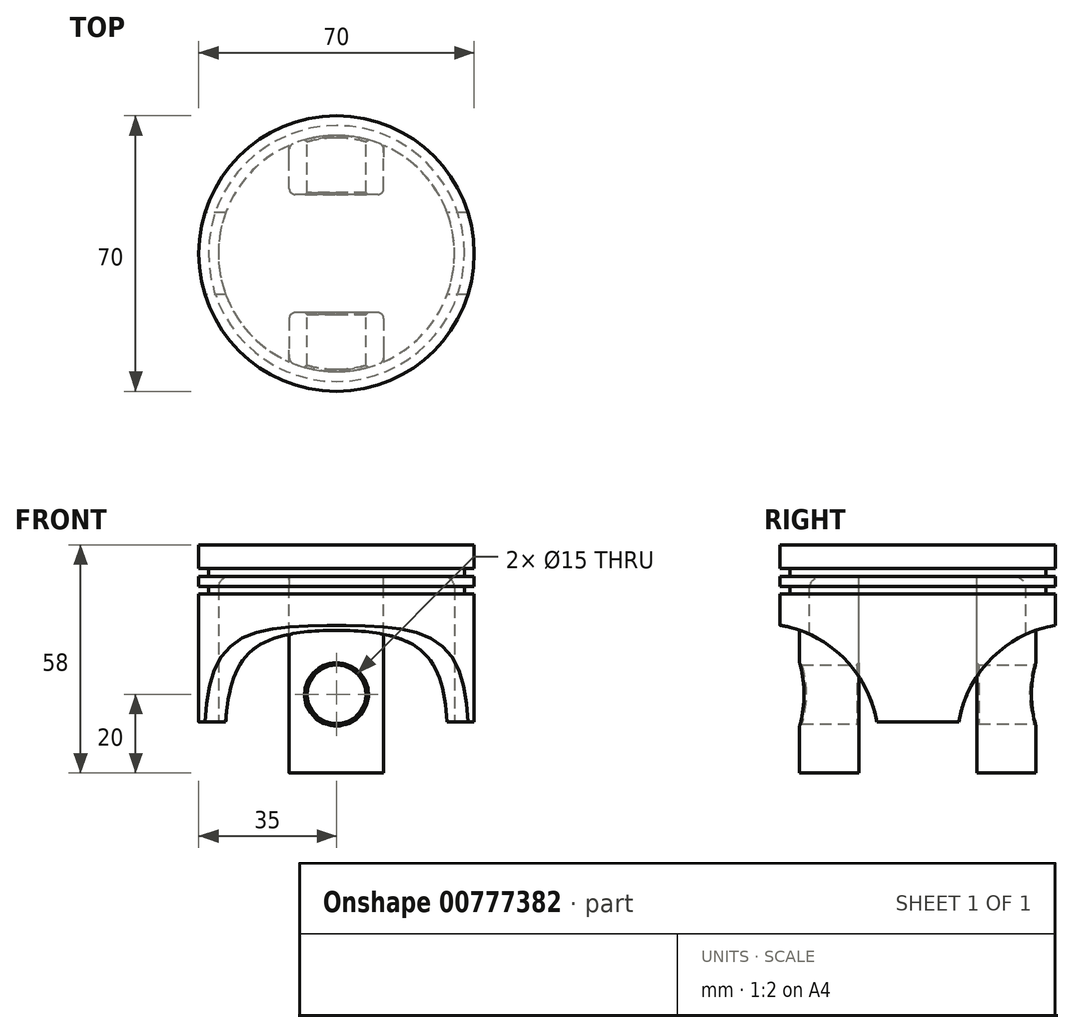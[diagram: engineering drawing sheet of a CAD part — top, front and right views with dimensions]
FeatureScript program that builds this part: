
annotation { "Feature Type Name" : "Feature", "Feature Type Description" : "" }
export const myFeature = defineFeature(function(context is Context, id is Id, definition is map)
    precondition{}
    {
        {
            var Q0;
            Q0=qCreatedBy(makeId("Front.planeOp"),FACE);
            var sketch = newSketch(context, id + "F0", { "sketchPlane" : qUnion([Q0])});
            skLineSegment(sketch, "E0", {"start": v(0, 0) * mm, "end": v(0, 45) * mm});
            skLineSegment(sketch, "E1", {"start": v(0, 45) * mm, "end": v(-35, 45) * mm});
            skLineSegment(sketch, "E2", {"start": v(-35, 45) * mm, "end": v(-35, 39) * mm});
            skLineSegment(sketch, "E3", {"start": v(-35, 0) * mm, "end": v(-30, 0) * mm});
            skLineSegment(sketch, "E4", {"start": v(-30, 0) * mm, "end": v(-30, 37) * mm});
            skLineSegment(sketch, "E5", {"start": v(-30, 37) * mm, "end": v(0, 37) * mm});
            skLineSegment(sketch, "E6", {"start": v(-35, 39) * mm, "end": v(-32.5, 39) * mm});
            skLineSegment(sketch, "E7", {"start": v(-32.5, 39) * mm, "end": v(-32.5, 37) * mm});
            skLineSegment(sketch, "E8", {"start": v(-32.5, 37) * mm, "end": v(-35, 37) * mm});
            skLineSegment(sketch, "E9", {"start": v(-35, 34.47) * mm, "end": v(-32.5, 34.47) * mm});
            skLineSegment(sketch, "E10", {"start": v(-32.5, 34.47) * mm, "end": v(-32.5, 32.47) * mm});
            skLineSegment(sketch, "E11", {"start": v(-32.5, 32.47) * mm, "end": v(-35, 32.47) * mm});
            skLineSegment(sketch, "E12.trimOffspring", {"start": v(-35, 32.47) * mm, "end": v(-35, 0) * mm});
            skLineSegment(sketch, "E13.trimOffspring", {"start": v(-35, 37) * mm, "end": v(-35, 34.47) * mm});
            skSolve(sketch);
        }
        {
            var Q0;
            Q0 = qSketchRegion(id + "F0", true);
            var Q1;
            Q1=sQuery(id+"F0.wireOp",EDGE,"E0");
            revolve(context, id + "F1", {"surfaceOperationType" : NewSurfaceOperationType.NEW, "entities" : qUnion([Q0]), "axis" : qUnion([Q1]), "revolveType" : RevolveType.FULL});
        }
        {
            var Q0;
            Q0=qCreatedBy(makeId("Right.planeOp"),FACE);
            var sketch = newSketch(context, id + "F2", { "sketchPlane" : qUnion([Q0])});
            skLineSegment(sketch, "E14", {"start": v(0, 0) * mm, "end": v(35, 0) * mm, "construction": true});
            skCircle(sketch, "E15", {"center": v(40, -5) * mm, "radius": 30 * mm});
            skLineSegment(sketch, "E16", {"start": v(0, 0) * mm, "end": v(0, 45) * mm, "construction": true});
            skCircle(sketch, "E17.MirrorC", {"center": v(-40, -5) * mm, "radius": 30 * mm});
            skSolve(sketch);
        }
        {
            var Q0;
            Q0 = qSketchRegion(id + "F2", true);
            extrude(context, id + "F3", {"entities" : qUnion([Q0]), "operationType" : NewBodyOperationType.REMOVE, "endBound" : BoundingType.THROUGH_ALL, "depth" : 80 * mm, "offsetDistance" : 25 * mm, "hasSecondDirection" : true, "secondDirectionBound" : BoundingType.THROUGH_ALL, "secondDirectionOppositeDirection" : true, "secondDirectionDepth" : 25 * mm});
        }
        {
            var Q0;
            Q0=makeQuery(id+"F1.opRevolve","SWEPT_FACE",FACE,{"disambiguationData":[OSD([sQuery(id+"F0.wireOp",EDGE,"E5")])]});
            var sketch = newSketch(context, id + "F4", { "sketchPlane" : qUnion([Q0])});
            skLineSegment(sketch, "E18", {"start": v(0, 0) * mm, "end": v(0, 30) * mm, "construction": true});
            skLineSegment(sketch, "E19", {"start": v(0, 0) * mm, "end": v(0, -30) * mm, "construction": true});
            skLineSegment(sketch, "E20", {"start": v(0, 0) * mm, "end": v(-30, 0) * mm, "construction": true});
            skLineSegment(sketch, "E21", {"start": v(0, 0) * mm, "end": v(30, 0) * mm, "construction": true});
            skLineSegment(sketch, "E22", {"start": v(0, 15) * mm, "end": v(-12, 15) * mm});
            skLineSegment(sketch, "E23", {"start": v(-12, 15) * mm, "end": v(-12, 27.5) * mm});
            skLineSegment(sketch, "E24.MirrorCS", {"start": v(0, 15) * mm, "end": v(12, 15) * mm});
            skLineSegment(sketch, "E25.MirrorCS", {"start": v(12, 15) * mm, "end": v(12, 27.5) * mm});
            skLineSegment(sketch, "E26.MirrorCS", {"start": v(0, -15) * mm, "end": v(12, -15) * mm});
            skLineSegment(sketch, "E27.MirrorCS", {"start": v(0, -15) * mm, "end": v(-12, -15) * mm});
            skLineSegment(sketch, "E28.MirrorCS", {"start": v(-12, -15) * mm, "end": v(-12, -27.5) * mm});
            skLineSegment(sketch, "E29.MirrorCS", {"start": v(12, -15) * mm, "end": v(12, -27.5) * mm});
            skSolve(sketch);
        }
        {
            var Q0;
            Q0=makeQuery(id+"F4.imprint","IMPRINT",FACE,{"disambiguationData":[TD([[makeQuery(id+"F4.imprint","IMPRINT",EDGE,{"derivedFrom":sQuery(id+"F4.wireOp",EDGE,"E22")}),-1.0]])]});
            var Q1;
            Q1=makeQuery(id+"F4.imprint","IMPRINT",FACE,{"disambiguationData":[TD([[makeQuery(id+"F4.imprint","IMPRINT",EDGE,{"derivedFrom":sQuery(id+"F4.wireOp",EDGE,"E26.MirrorCS")}),-1.0]])]});
            extrude(context, id + "F5", {"entities" : qUnion([Q0, Q1]), "operationType" : NewBodyOperationType.ADD, "depth" : 50 * mm, "offsetDistance" : 25 * mm});
        }
        {
            var Q0;
            Q0=makeQuery(id+"F5.opExtrude","SWEPT_FACE",FACE,{"disambiguationData":[OSD([sQuery(id+"F4.wireOp",EDGE,"E22"),sQuery(id+"F4.wireOp",EDGE,"E24.MirrorCS")])]});
            var sketch = newSketch(context, id + "F6", { "sketchPlane" : qUnion([Q0])});
            skCircle(sketch, "E30", {"center": v(0, 7) * mm, "radius": 7.5 * mm});
            skCircle(sketch, "E31", {"center": v(0, 7) * mm, "radius": 12 * mm});
            skSolve(sketch);
        }
        {
            var Q0;
            Q0=makeQuery(id+"F6.imprint","IMPRINT",FACE,{"disambiguationData":[TD([[makeQuery(id+"F6.imprint","IMPRINT",EDGE,{"derivedFrom":sQuery(id+"F6.wireOp",EDGE,"E30")}),1.0]])]});
            var Q1;
            {var subQ1=sQuery(id+"F4.wireOp",EDGE,"E22");var subQ4=sQuery(id+"F4.wireOp",EDGE,"E24.MirrorCS");var subQ7=makeQuery(id+"F5.opExtrude","CAP_EDGE",EDGE,{"disambiguationData":[OSD([subQ1,subQ4])],"isStart":false});Q1=makeQuery(id+"F6.imprint","IMPRINT",FACE,{"disambiguationData":[TD([[makeQuery(id+"F6.imprint","IMPRINT",EDGE,{"derivedFrom":subQ7}),-1.0]])]});}
            extrude(context, id + "F7", {"entities" : qUnion([Q0, Q1]), "operationType" : NewBodyOperationType.REMOVE, "oppositeDirection" : true, "depth" : 200 * mm, "offsetDistance" : 25 * mm, "symmetric" : true});
        }
        {
            var Q0;
            {var subQ0=sQuery(id+"F0.wireOp",EDGE,"E4");var subQ1=sQuery(id+"F0.wireOp",EDGE,"E5");Q0=makeQuery(id+"F5.boolean.opBoolean","SPLIT",EDGE,{"disambiguationData":[TD([makeQuery(id+"F5.opExtrude","SWEPT_FACE",FACE,{"disambiguationData":[OSD([sQuery(id+"F4.wireOp",EDGE,"E23")])]})])],"derivedFrom":makeQuery(id+"F1.opRevolve","SWEPT_EDGE",EDGE,{"disambiguationData":[OSD([subQ0,subQ1])]})});}
            var Q1;
            {var subQ0=sQuery(id+"F0.wireOp",EDGE,"E4");var subQ1=sQuery(id+"F0.wireOp",EDGE,"E5");Q1=makeQuery(id+"F5.boolean.opBoolean","SPLIT",EDGE,{"disambiguationData":[TD([makeQuery(id+"F5.opExtrude","SWEPT_FACE",FACE,{"disambiguationData":[OSD([sQuery(id+"F4.wireOp",EDGE,"E25.MirrorCS")])]})])],"derivedFrom":makeQuery(id+"F1.opRevolve","SWEPT_EDGE",EDGE,{"disambiguationData":[OSD([subQ0,subQ1])]})});}
            var Q2;
            Q2=makeQuery(id+"F5.opExtrude","CAP_EDGE",EDGE,{"disambiguationData":[OSD([sQuery(id+"F4.wireOp",EDGE,"E22"),sQuery(id+"F4.wireOp",EDGE,"E24.MirrorCS")])],"isStart":true});
            var Q3;
            Q3=makeQuery(id+"F5.opExtrude","CAP_EDGE",EDGE,{"disambiguationData":[OSD([sQuery(id+"F4.wireOp",EDGE,"E28.MirrorCS")])],"isStart":true});
            var Q4;
            Q4=makeQuery(id+"F5.opExtrude","CAP_EDGE",EDGE,{"disambiguationData":[OSD([sQuery(id+"F4.wireOp",EDGE,"E26.MirrorCS"),sQuery(id+"F4.wireOp",EDGE,"E27.MirrorCS")])],"isStart":true});
            var Q5;
            Q5=makeQuery(id+"F5.opExtrude","CAP_EDGE",EDGE,{"disambiguationData":[OSD([sQuery(id+"F4.wireOp",EDGE,"E29.MirrorCS")])],"isStart":true});
            var Q6;
            Q6=makeQuery(id+"F5.opExtrude","CAP_EDGE",EDGE,{"disambiguationData":[OSD([sQuery(id+"F4.wireOp",EDGE,"E25.MirrorCS")])],"isStart":true});
            var Q7;
            Q7=makeQuery(id+"F5.opExtrude","CAP_EDGE",EDGE,{"disambiguationData":[OSD([sQuery(id+"F4.wireOp",EDGE,"E23")])],"isStart":true});
            fillet(context, id + "F8", {"entities" : qUnion([Q0, Q1, Q2, Q3, Q4, Q5, Q6, Q7]), "radius" : 3 * mm, "tangentPropagation" : true, "allowEdgeOverflow" : false});
        }
        {
            var Q0;
            Q0=makeQuery(id+"F7.boolean.opBoolean","INTERSECT",EDGE,{"derivedFrom":[makeQuery(id+"F5.opExtrude","SWEPT_FACE",FACE,{"disambiguationData":[OSD([sQuery(id+"F4.wireOp",EDGE,"E26.MirrorCS"),sQuery(id+"F4.wireOp",EDGE,"E27.MirrorCS")])]}),makeQuery(id+"F7.opExtrude","SWEPT_FACE",FACE,{"disambiguationData":[OSD([sQuery(id+"F6.wireOp",EDGE,"E31")])]})]});
            var Q1;
            Q1=makeQuery(id+"F7.boolean.opBoolean","INTERSECT",EDGE,{"derivedFrom":[makeQuery(id+"F5.opExtrude","SWEPT_FACE",FACE,{"disambiguationData":[OSD([sQuery(id+"F4.wireOp",EDGE,"E22"),sQuery(id+"F4.wireOp",EDGE,"E24.MirrorCS")])]}),makeQuery(id+"F7.opExtrude","SWEPT_FACE",FACE,{"disambiguationData":[OSD([sQuery(id+"F6.wireOp",EDGE,"E31")])]})]});
            var Q2;
            Q2=makeQuery(id+"F5.opExtrude","SWEPT_EDGE",EDGE,{"disambiguationData":[OSD([sQuery(id+"F4.wireOp",EDGE,"E27.MirrorCS"),sQuery(id+"F4.wireOp",EDGE,"E28.MirrorCS")])]});
            var Q3;
            Q3=makeQuery(id+"F5.opExtrude","SWEPT_EDGE",EDGE,{"disambiguationData":[OSD([sQuery(id+"F4.wireOp",EDGE,"E22"),sQuery(id+"F4.wireOp",EDGE,"E23")])]});
            var Q4;
            {var subQ0=sQuery(id+"F0.wireOp",EDGE,"E5");var subQ1=sQuery(id+"F0.wireOp",EDGE,"E4");var subQ2=makeQuery(id+"F1.opRevolve","SWEPT_EDGE",EDGE,{"disambiguationData":[OSD([subQ1,subQ0])]});Q4=makeQuery(id+"F7.boolean.opBoolean","INTERSECT",EDGE,{"derivedFrom":[makeQuery(id+"F5.opExtrude","SWEPT_FACE",FACE,{"disambiguationData":[OSD([subQ1,subQ0]),TDD([makeQuery(id+"F4.imprint","IMPRINT",EDGE,{"disambiguationData":[TD([[makeQuery(id+"F4.imprint","INTERSECT",VERTEX,{"derivedFrom":[subQ2,sQuery(id+"F4.wireOp",EDGE,"E23")]}),1.0]])],"derivedFrom":subQ2})])]}),makeQuery(id+"F7.opExtrude","SWEPT_FACE",FACE,{"disambiguationData":[OSD([sQuery(id+"F6.wireOp",EDGE,"E31")])]})]});}
            var Q5;
            {var subQ0=sQuery(id+"F4.wireOp",EDGE,"E23");var subQ1=sQuery(id+"F0.wireOp",EDGE,"E5");var subQ2=sQuery(id+"F0.wireOp",EDGE,"E4");var subQ3=makeQuery(id+"F1.opRevolve","SWEPT_EDGE",EDGE,{"disambiguationData":[OSD([subQ2,subQ1])]});Q5=makeQuery(id+"F5.boolean.opBoolean","SPLIT",EDGE,{"disambiguationData":[topologyDisambiguationEdgeConnected([makeQuery(id+"F5.opExtrude","SWEPT_FACE",FACE,{"disambiguationData":[OSD([subQ2,subQ1]),TDD([makeQuery(id+"F4.imprint","IMPRINT",EDGE,{"disambiguationData":[TD([[makeQuery(id+"F4.imprint","INTERSECT",VERTEX,{"derivedFrom":[subQ3,subQ0]}),1.0]])],"derivedFrom":subQ3})])]})])],"derivedFrom":makeQuery(id+"F5.opExtrude","SWEPT_EDGE",EDGE,{"disambiguationData":[OSD([subQ2,subQ1,subQ0])]})});}
            var Q6;
            {var subQ0=sQuery(id+"F4.wireOp",EDGE,"E28.MirrorCS");var subQ1=sQuery(id+"F0.wireOp",EDGE,"E5");var subQ2=sQuery(id+"F0.wireOp",EDGE,"E4");var subQ3=makeQuery(id+"F1.opRevolve","SWEPT_EDGE",EDGE,{"disambiguationData":[OSD([subQ2,subQ1])]});Q6=makeQuery(id+"F5.boolean.opBoolean","SPLIT",EDGE,{"disambiguationData":[topologyDisambiguationEdgeConnected([makeQuery(id+"F5.opExtrude","SWEPT_FACE",FACE,{"disambiguationData":[OSD([subQ2,subQ1]),TDD([makeQuery(id+"F4.imprint","IMPRINT",EDGE,{"disambiguationData":[TD([[makeQuery(id+"F4.imprint","INTERSECT",VERTEX,{"derivedFrom":[subQ3,subQ0]}),-1.0]])],"derivedFrom":subQ3})])]})])],"derivedFrom":makeQuery(id+"F5.opExtrude","SWEPT_EDGE",EDGE,{"disambiguationData":[OSD([subQ2,subQ1,subQ0])]})});}
            var Q7;
            {var subQ0=sQuery(id+"F0.wireOp",EDGE,"E5");var subQ1=sQuery(id+"F0.wireOp",EDGE,"E4");var subQ2=makeQuery(id+"F1.opRevolve","SWEPT_EDGE",EDGE,{"disambiguationData":[OSD([subQ1,subQ0])]});Q7=makeQuery(id+"F7.boolean.opBoolean","INTERSECT",EDGE,{"derivedFrom":[makeQuery(id+"F5.opExtrude","SWEPT_FACE",FACE,{"disambiguationData":[OSD([subQ1,subQ0]),TDD([makeQuery(id+"F4.imprint","IMPRINT",EDGE,{"disambiguationData":[TD([[makeQuery(id+"F4.imprint","INTERSECT",VERTEX,{"derivedFrom":[subQ2,sQuery(id+"F4.wireOp",EDGE,"E28.MirrorCS")]}),-1.0]])],"derivedFrom":subQ2})])]}),makeQuery(id+"F7.opExtrude","SWEPT_FACE",FACE,{"disambiguationData":[OSD([sQuery(id+"F6.wireOp",EDGE,"E31")])]})]});}
            var Q8;
            {var subQ0=sQuery(id+"F4.wireOp",EDGE,"E25.MirrorCS");var subQ1=sQuery(id+"F0.wireOp",EDGE,"E5");var subQ2=sQuery(id+"F0.wireOp",EDGE,"E4");var subQ3=makeQuery(id+"F1.opRevolve","SWEPT_EDGE",EDGE,{"disambiguationData":[OSD([subQ2,subQ1])]});Q8=makeQuery(id+"F5.boolean.opBoolean","SPLIT",EDGE,{"disambiguationData":[topologyDisambiguationEdgeConnected([makeQuery(id+"F5.opExtrude","SWEPT_FACE",FACE,{"disambiguationData":[OSD([subQ2,subQ1]),TDD([makeQuery(id+"F4.imprint","IMPRINT",EDGE,{"disambiguationData":[TD([[makeQuery(id+"F4.imprint","INTERSECT",VERTEX,{"derivedFrom":[subQ3,sQuery(id+"F4.wireOp",EDGE,"E23")]}),1.0]])],"derivedFrom":subQ3})])]})])],"derivedFrom":makeQuery(id+"F5.opExtrude","SWEPT_EDGE",EDGE,{"disambiguationData":[OSD([subQ2,subQ1,subQ0])]})});}
            var Q9;
            Q9=makeQuery(id+"F5.opExtrude","SWEPT_EDGE",EDGE,{"disambiguationData":[OSD([sQuery(id+"F4.wireOp",EDGE,"E26.MirrorCS"),sQuery(id+"F4.wireOp",EDGE,"E29.MirrorCS")])]});
            var Q10;
            Q10=makeQuery(id+"F5.opExtrude","SWEPT_EDGE",EDGE,{"disambiguationData":[OSD([sQuery(id+"F4.wireOp",EDGE,"E24.MirrorCS"),sQuery(id+"F4.wireOp",EDGE,"E25.MirrorCS")])]});
            var Q11;
            {var subQ0=sQuery(id+"F4.wireOp",EDGE,"E29.MirrorCS");var subQ1=sQuery(id+"F0.wireOp",EDGE,"E5");var subQ2=sQuery(id+"F0.wireOp",EDGE,"E4");var subQ3=makeQuery(id+"F1.opRevolve","SWEPT_EDGE",EDGE,{"disambiguationData":[OSD([subQ2,subQ1])]});Q11=makeQuery(id+"F5.boolean.opBoolean","SPLIT",EDGE,{"disambiguationData":[topologyDisambiguationEdgeConnected([makeQuery(id+"F5.opExtrude","SWEPT_FACE",FACE,{"disambiguationData":[OSD([subQ2,subQ1]),TDD([makeQuery(id+"F4.imprint","IMPRINT",EDGE,{"disambiguationData":[TD([[makeQuery(id+"F4.imprint","INTERSECT",VERTEX,{"derivedFrom":[subQ3,sQuery(id+"F4.wireOp",EDGE,"E28.MirrorCS")]}),-1.0]])],"derivedFrom":subQ3})])]})])],"derivedFrom":makeQuery(id+"F5.opExtrude","SWEPT_EDGE",EDGE,{"disambiguationData":[OSD([subQ2,subQ1,subQ0])]})});}
            fillet(context, id + "F9", {"entities" : qUnion([Q0, Q1, Q2, Q3, Q4, Q5, Q6, Q7, Q8, Q9, Q10, Q11]), "radius" : 1.5 * mm, "tangentPropagation" : true, "allowEdgeOverflow" : false});
        }
        {
            var Q0;
            {var subQ0=sQuery(id+"F0.wireOp",EDGE,"E5");var subQ1=sQuery(id+"F0.wireOp",EDGE,"E4");var subQ2=makeQuery(id+"F1.opRevolve","SWEPT_EDGE",EDGE,{"disambiguationData":[OSD([subQ1,subQ0])]});Q0=makeQuery(id+"F7.boolean.opBoolean","INTERSECT",EDGE,{"derivedFrom":[makeQuery(id+"F5.opExtrude","SWEPT_FACE",FACE,{"disambiguationData":[OSD([subQ1,subQ0]),TDD([makeQuery(id+"F4.imprint","IMPRINT",EDGE,{"disambiguationData":[TD([[makeQuery(id+"F4.imprint","INTERSECT",VERTEX,{"derivedFrom":[subQ2,sQuery(id+"F4.wireOp",EDGE,"E23")]}),1.0]])],"derivedFrom":subQ2})])]}),makeQuery(id+"F7.opExtrude","SWEPT_FACE",FACE,{"disambiguationData":[OSD([sQuery(id+"F6.wireOp",EDGE,"E30")])]})]});}
            var Q1;
            Q1=makeQuery(id+"F7.boolean.opBoolean","INTERSECT",EDGE,{"derivedFrom":[makeQuery(id+"F5.opExtrude","SWEPT_FACE",FACE,{"disambiguationData":[OSD([sQuery(id+"F4.wireOp",EDGE,"E22"),sQuery(id+"F4.wireOp",EDGE,"E24.MirrorCS")])]}),makeQuery(id+"F7.opExtrude","SWEPT_FACE",FACE,{"disambiguationData":[OSD([sQuery(id+"F6.wireOp",EDGE,"E30")])]})]});
            var Q2;
            {var subQ0=sQuery(id+"F0.wireOp",EDGE,"E5");var subQ1=sQuery(id+"F0.wireOp",EDGE,"E4");var subQ2=makeQuery(id+"F1.opRevolve","SWEPT_EDGE",EDGE,{"disambiguationData":[OSD([subQ1,subQ0])]});Q2=makeQuery(id+"F7.boolean.opBoolean","INTERSECT",EDGE,{"derivedFrom":[makeQuery(id+"F5.opExtrude","SWEPT_FACE",FACE,{"disambiguationData":[OSD([subQ1,subQ0]),TDD([makeQuery(id+"F4.imprint","IMPRINT",EDGE,{"disambiguationData":[TD([[makeQuery(id+"F4.imprint","INTERSECT",VERTEX,{"derivedFrom":[subQ2,sQuery(id+"F4.wireOp",EDGE,"E28.MirrorCS")]}),-1.0]])],"derivedFrom":subQ2})])]}),makeQuery(id+"F7.opExtrude","SWEPT_FACE",FACE,{"disambiguationData":[OSD([sQuery(id+"F6.wireOp",EDGE,"E30")])]})]});}
            var Q3;
            Q3=makeQuery(id+"F7.boolean.opBoolean","INTERSECT",EDGE,{"derivedFrom":[makeQuery(id+"F5.opExtrude","SWEPT_FACE",FACE,{"disambiguationData":[OSD([sQuery(id+"F4.wireOp",EDGE,"E26.MirrorCS"),sQuery(id+"F4.wireOp",EDGE,"E27.MirrorCS")])]}),makeQuery(id+"F7.opExtrude","SWEPT_FACE",FACE,{"disambiguationData":[OSD([sQuery(id+"F6.wireOp",EDGE,"E30")])]})]});
            chamfer(context, id + "F10", {"entities" : qUnion([Q0, Q1, Q2, Q3]), "width" : .5 * mm, "tangentPropagation" : true});
        }
    });
